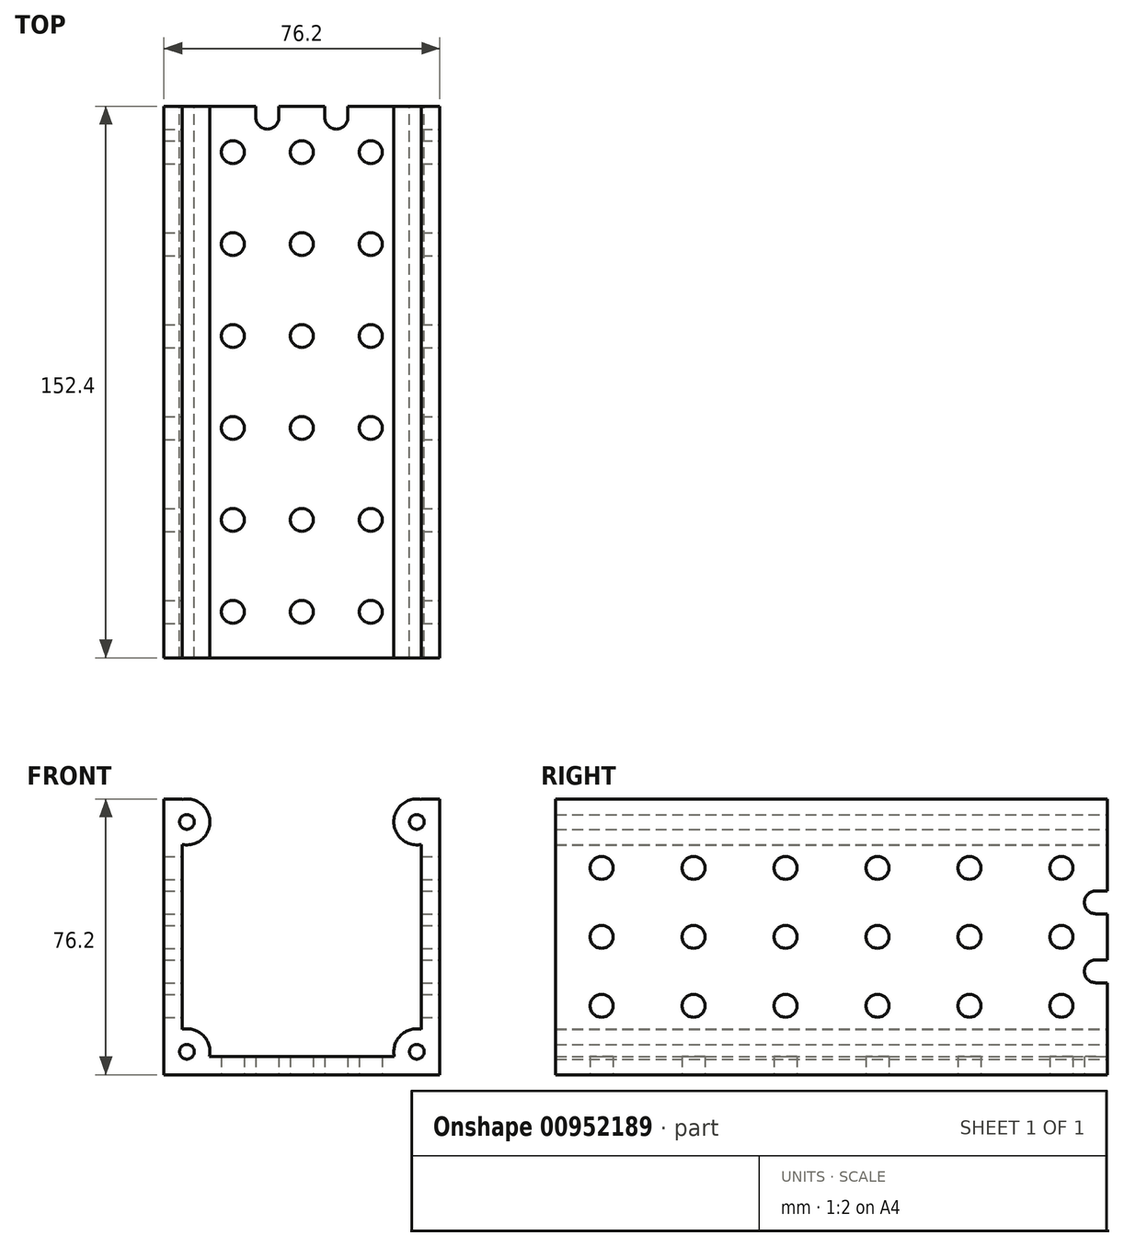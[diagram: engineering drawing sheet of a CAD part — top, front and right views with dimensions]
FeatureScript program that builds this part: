
annotation { "Feature Type Name" : "Feature", "Feature Type Description" : "" }
export const myFeature = defineFeature(function(context is Context, id is Id, definition is map)
    precondition{}
    {
        {
            var Q0;
            Q0=qCreatedBy(makeId("Front.planeOp"),FACE);
            var sketch = newSketch(context, id + "F0", { "sketchPlane" : qUnion([Q0])});
            skLineSegment(sketch, "E0.bottom", {"start": v(-38.1, 0) * mm, "end": v(38.1, 0) * mm});
            skLineSegment(sketch, "E0.top", {"start": v(-38.1, 76.2) * mm, "end": v(-33.02, 76.2) * mm});
            skLineSegment(sketch, "E0.left", {"start": v(-38.1, 0) * mm, "end": v(-38.1, 76.2) * mm});
            skLineSegment(sketch, "E0.right", {"start": v(38.1, 0) * mm, "end": v(38.1, 76.2) * mm});
            skLineSegment(sketch, "E1.top", {"start": v(-33.02, 5.08) * mm, "end": v(33.02, 5.08) * mm});
            skLineSegment(sketch, "E1.left", {"start": v(-33.02, 76.2) * mm, "end": v(-33.02, 5.08) * mm});
            skLineSegment(sketch, "E1.right", {"start": v(33.02, 76.2) * mm, "end": v(33.02, 5.08) * mm});
            skLineSegment(sketch, "E2.trimOffspring", {"start": v(33.02, 76.2) * mm, "end": v(38.1, 76.2) * mm});
            skSolve(sketch);
        }
        {
            var Q0;
            Q0=qCreatedBy(makeId("Front.planeOp"),FACE);
            var sketch = newSketch(context, id + "F1", { "sketchPlane" : qUnion([Q0])});
            skCircle(sketch, "E3", {"center": v(-31.75, 6.35) * mm, "radius": 6.35 * mm});
            skCircle(sketch, "E4", {"center": v(31.75, 6.35) * mm, "radius": 6.35 * mm});
            skCircle(sketch, "E5", {"center": v(-31.75, 69.85) * mm, "radius": 6.35 * mm});
            skCircle(sketch, "E6", {"center": v(31.75, 69.85) * mm, "radius": 6.35 * mm});
            skSolve(sketch);
        }
        {
            var Q0;
            Q0=qCreatedBy(makeId("Front.planeOp"),FACE);
            var sketch = newSketch(context, id + "F2", { "sketchPlane" : qUnion([Q0])});
            skCircle(sketch, "E7.0", {"center": v(-31.75, 69.85) * mm, "radius": 6.35 * mm, "construction": true});
            skCircle(sketch, "E8.0", {"center": v(31.75, 69.85) * mm, "radius": 6.35 * mm, "construction": true});
            skCircle(sketch, "E9.0", {"center": v(31.75, 6.35) * mm, "radius": 6.35 * mm, "construction": true});
            skCircle(sketch, "E10.0", {"center": v(-31.75, 6.35) * mm, "radius": 6.35 * mm, "construction": true});
            skCircle(sketch, "E11", {"center": v(-31.75, 69.85) * mm, "radius": 2.03 * mm});
            skCircle(sketch, "E12", {"center": v(31.75, 69.85) * mm, "radius": 2.03 * mm});
            skCircle(sketch, "E13", {"center": v(-31.75, 6.35) * mm, "radius": 2.03 * mm});
            skCircle(sketch, "E14", {"center": v(31.75, 6.35) * mm, "radius": 2.03 * mm});
            skSolve(sketch);
        }
        {
            var Q0;
            Q0 = qSketchRegion(id + "F0", true);
            extrude(context, id + "F3", {"entities" : qUnion([Q0]), "depth" : 152.4 * mm, "offsetDistance" : 25.4 * mm});
        }
        {
            var Q0;
            Q0 = qSketchRegion(id + "F1", true);
            extrude(context, id + "F4", {"entities" : qUnion([Q0]), "operationType" : NewBodyOperationType.ADD, "depth" : 152.4 * mm, "offsetDistance" : 25.4 * mm});
        }
        {
            var Q0;
            Q0 = qSketchRegion(id + "F2", true);
            extrude(context, id + "F5", {"entities" : qUnion([Q0]), "operationType" : NewBodyOperationType.REMOVE, "endBound" : BoundingType.THROUGH_ALL, "depth" : 25.4 * mm, "offsetDistance" : 25.4 * mm});
        }
        {
            var Q0;
            Q0=qCreatedBy(makeId("Right.planeOp"),FACE);
            var sketch = newSketch(context, id + "F6", { "sketchPlane" : qUnion([Q0])});
            skCircle(sketch, "E15", {"center": v(-12.7, 19.05) * mm, "radius": 3.18 * mm});
            skCircle(sketch, "E16.0.1.0", {"center": v(-12.7, 38.1) * mm, "radius": 3.18 * mm});
            skCircle(sketch, "E16.0.2.0", {"center": v(-12.7, 57.15) * mm, "radius": 3.18 * mm});
            skCircle(sketch, "E16.1.0.0", {"center": v(-38.1, 19.05) * mm, "radius": 3.18 * mm});
            skCircle(sketch, "E16.1.1.0", {"center": v(-38.1, 38.1) * mm, "radius": 3.18 * mm});
            skCircle(sketch, "E16.1.2.0", {"center": v(-38.1, 57.15) * mm, "radius": 3.18 * mm});
            skCircle(sketch, "E16.2.0.0", {"center": v(-63.5, 19.05) * mm, "radius": 3.18 * mm});
            skCircle(sketch, "E16.2.1.0", {"center": v(-63.5, 38.1) * mm, "radius": 3.18 * mm});
            skCircle(sketch, "E16.2.2.0", {"center": v(-63.5, 57.15) * mm, "radius": 3.18 * mm});
            skCircle(sketch, "E16.3.0.0", {"center": v(-88.9, 19.05) * mm, "radius": 3.18 * mm});
            skCircle(sketch, "E16.3.1.0", {"center": v(-88.9, 38.1) * mm, "radius": 3.18 * mm});
            skCircle(sketch, "E16.3.2.0", {"center": v(-88.9, 57.15) * mm, "radius": 3.18 * mm});
            skLineSegment(sketch, "E16.direction1", {"start": v(-12.7, 19.05) * mm, "end": v(-38.1, 19.05) * mm, "construction": true});
            skLineSegment(sketch, "E16.direction2", {"start": v(-12.7, 19.05) * mm, "end": v(-12.7, 38.1) * mm, "construction": true});
            skCircle(sketch, "E17.0.4.0", {"center": v(-114.3, 19.05) * mm, "radius": 3.18 * mm});
            skCircle(sketch, "E17.0.4.1", {"center": v(-114.3, 38.1) * mm, "radius": 3.18 * mm});
            skCircle(sketch, "E17.0.4.2", {"center": v(-114.3, 57.15) * mm, "radius": 3.18 * mm});
            skCircle(sketch, "E17.0.5.0", {"center": v(-139.7, 19.05) * mm, "radius": 3.18 * mm});
            skCircle(sketch, "E17.0.5.1", {"center": v(-139.7, 38.1) * mm, "radius": 3.18 * mm});
            skCircle(sketch, "E17.0.5.2", {"center": v(-139.7, 57.15) * mm, "radius": 3.18 * mm});
            skSolve(sketch);
        }
        {
            var Q0;
            Q0 = qSketchRegion(id + "F6", true);
            extrude(context, id + "F7", {"entities" : qUnion([Q0]), "operationType" : NewBodyOperationType.REMOVE, "endBound" : BoundingType.THROUGH_ALL, "oppositeDirection" : true, "depth" : 25.4 * mm, "offsetDistance" : 25.4 * mm, "hasSecondDirection" : true, "secondDirectionBound" : SecondDirectionBoundingType.THROUGH_ALL, "secondDirectionOppositeDirection" : false, "secondDirectionDepth" : 25.4 * mm});
        }
        {
            var Q0;
            Q0=qCreatedBy(makeId("Top.planeOp"),FACE);
            var sketch = newSketch(context, id + "F8", { "sketchPlane" : qUnion([Q0])});
            skCircle(sketch, "E18", {"center": v(-19.05, -12.7) * mm, "radius": 3.18 * mm});
            skCircle(sketch, "E19.0.1.0", {"center": v(-19.05, -38.1) * mm, "radius": 3.18 * mm});
            skCircle(sketch, "E19.0.2.0", {"center": v(-19.05, -63.5) * mm, "radius": 3.18 * mm});
            skCircle(sketch, "E19.0.3.0", {"center": v(-19.05, -88.9) * mm, "radius": 3.18 * mm});
            skCircle(sketch, "E19.1.0.0", {"center": v(0, -12.7) * mm, "radius": 3.18 * mm});
            skCircle(sketch, "E19.1.1.0", {"center": v(0, -38.1) * mm, "radius": 3.18 * mm});
            skCircle(sketch, "E19.1.2.0", {"center": v(0, -63.5) * mm, "radius": 3.18 * mm});
            skCircle(sketch, "E19.1.3.0", {"center": v(0, -88.9) * mm, "radius": 3.18 * mm});
            skCircle(sketch, "E19.2.0.0", {"center": v(19.05, -12.7) * mm, "radius": 3.18 * mm});
            skCircle(sketch, "E19.2.1.0", {"center": v(19.05, -38.1) * mm, "radius": 3.18 * mm});
            skCircle(sketch, "E19.2.2.0", {"center": v(19.05, -63.5) * mm, "radius": 3.18 * mm});
            skCircle(sketch, "E19.2.3.0", {"center": v(19.05, -88.9) * mm, "radius": 3.18 * mm});
            skLineSegment(sketch, "E19.direction1", {"start": v(-19.05, -12.7) * mm, "end": v(0, -12.7) * mm, "construction": true});
            skLineSegment(sketch, "E19.direction2", {"start": v(-19.05, -12.7) * mm, "end": v(-19.05, -38.1) * mm, "construction": true});
            skCircle(sketch, "E20.0.0.4", {"center": v(-19.05, -114.3) * mm, "radius": 3.18 * mm});
            skCircle(sketch, "E20.0.0.5", {"center": v(-19.05, -139.7) * mm, "radius": 3.18 * mm});
            skCircle(sketch, "E20.0.1.4", {"center": v(0, -114.3) * mm, "radius": 3.18 * mm});
            skCircle(sketch, "E20.0.1.5", {"center": v(0, -139.7) * mm, "radius": 3.18 * mm});
            skCircle(sketch, "E20.0.2.4", {"center": v(19.05, -114.3) * mm, "radius": 3.18 * mm});
            skCircle(sketch, "E20.0.2.5", {"center": v(19.05, -139.7) * mm, "radius": 3.18 * mm});
            skSolve(sketch);
        }
        {
            var Q0;
            Q0 = qSketchRegion(id + "F8", true);
            extrude(context, id + "F9", {"entities" : qUnion([Q0]), "operationType" : NewBodyOperationType.REMOVE, "endBound" : BoundingType.THROUGH_ALL, "depth" : 25.4 * mm, "offsetDistance" : 25.4 * mm});
        }
        {
            var Q0;
            Q0=qCreatedBy(makeId("Right.planeOp"),FACE);
            var sketch = newSketch(context, id + "F10", { "sketchPlane" : qUnion([Q0])});
            skLineSegment(sketch, "E21.bottom", {"start": v(0, 50.8) * mm, "end": v(-3.18, 50.8) * mm});
            skLineSegment(sketch, "E21.top", {"start": v(0, 44.45) * mm, "end": v(-3.17, 44.45) * mm});
            skLineSegment(sketch, "E21.left", {"start": v(0, 50.8) * mm, "end": v(0, 44.45) * mm});
            skLineSegment(sketch, "E22.bottom", {"start": v(0, 31.75) * mm, "end": v(-3.17, 31.75) * mm});
            skLineSegment(sketch, "E22.top", {"start": v(0, 25.4) * mm, "end": v(-3.17, 25.4) * mm});
            skLineSegment(sketch, "E22.left", {"start": v(0, 31.75) * mm, "end": v(0, 25.4) * mm});
            skArc(sketch, "E23", {"start": v(-3.18, 50.8) * mm, "mid": v(-6.35, 47.63) * mm, "end": v(-3.18, 44.45) * mm});
            skArc(sketch, "E24", {"start": v(-3.17, 31.75) * mm, "mid": v(-6.35, 28.57) * mm, "end": v(-3.17, 25.4) * mm});
            skSolve(sketch);
        }
        {
            var Q0;
            Q0 = qSketchRegion(id + "F10", true);
            extrude(context, id + "F11", {"entities" : qUnion([Q0]), "operationType" : NewBodyOperationType.REMOVE, "endBound" : BoundingType.THROUGH_ALL, "oppositeDirection" : true, "depth" : 25.4 * mm, "offsetDistance" : 25.4 * mm, "hasSecondDirection" : true, "secondDirectionBound" : SecondDirectionBoundingType.THROUGH_ALL, "secondDirectionOppositeDirection" : false, "secondDirectionDepth" : 25.4 * mm});
        }
        {
            var Q0;
            Q0=qCreatedBy(makeId("Top.planeOp"),FACE);
            var sketch = newSketch(context, id + "F12", { "sketchPlane" : qUnion([Q0])});
            skLineSegment(sketch, "E25.bottom", {"start": v(-12.7, 0) * mm, "end": v(-6.35, 0) * mm});
            skLineSegment(sketch, "E25.left", {"start": v(-12.7, 0) * mm, "end": v(-12.7, -3.18) * mm});
            skLineSegment(sketch, "E25.right", {"start": v(-6.35, 0) * mm, "end": v(-6.35, -3.17) * mm});
            skLineSegment(sketch, "E26.bottom", {"start": v(6.35, 0) * mm, "end": v(12.7, 0) * mm});
            skLineSegment(sketch, "E26.left", {"start": v(6.35, 0) * mm, "end": v(6.35, -3.17) * mm});
            skLineSegment(sketch, "E26.right", {"start": v(12.7, 0) * mm, "end": v(12.7, -3.17) * mm});
            skArc(sketch, "E27", {"start": v(-12.7, -3.18) * mm, "mid": v(-9.53, -6.35) * mm, "end": v(-6.35, -3.18) * mm});
            skArc(sketch, "E28", {"start": v(6.35, -3.17) * mm, "mid": v(9.53, -6.35) * mm, "end": v(12.7, -3.17) * mm});
            skSolve(sketch);
        }
        {
            var Q0;
            Q0 = qSketchRegion(id + "F12", true);
            extrude(context, id + "F13", {"entities" : qUnion([Q0]), "operationType" : NewBodyOperationType.REMOVE, "endBound" : BoundingType.THROUGH_ALL, "depth" : 25.4 * mm, "offsetDistance" : 25.4 * mm});
        }
    });
